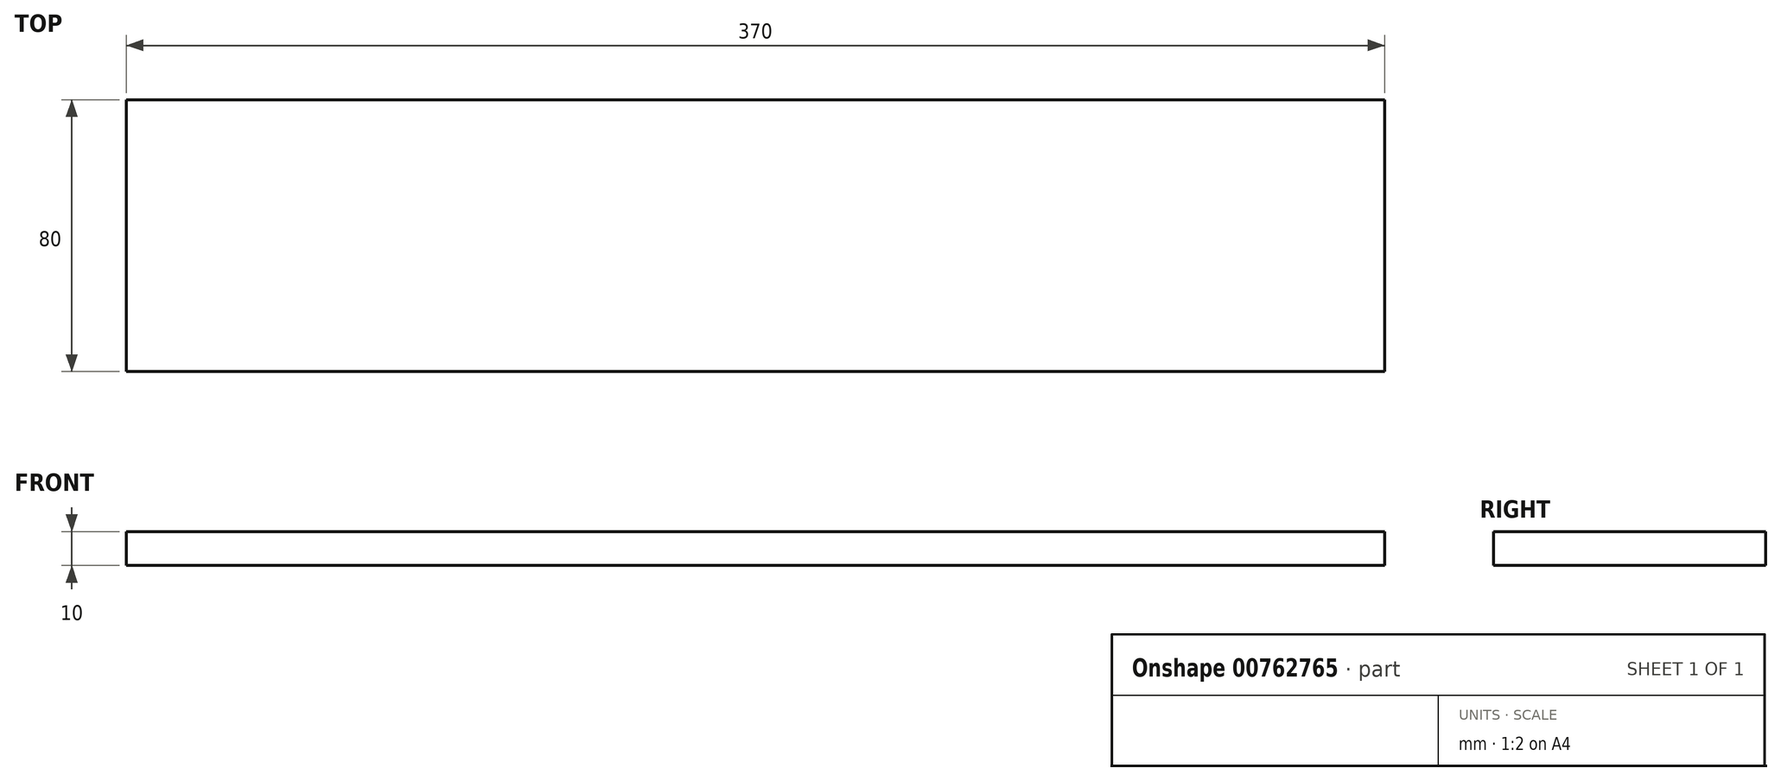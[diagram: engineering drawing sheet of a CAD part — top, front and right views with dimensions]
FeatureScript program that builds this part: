
annotation { "Feature Type Name" : "Feature", "Feature Type Description" : "" }
export const myFeature = defineFeature(function(context is Context, id is Id, definition is map)
    precondition{}
    {
        {
            var Q0;
            Q0=qCreatedBy(makeId("Top.planeOp"),FACE);
            var sketch = newSketch(context, id + "F0", { "sketchPlane" : qUnion([Q0])});
            skLineSegment(sketch, "E0.bottom", {"start": v(185, 40) * mm, "end": v(-185, 40) * mm});
            skLineSegment(sketch, "E0.top", {"start": v(185, -40) * mm, "end": v(-185, -40) * mm});
            skLineSegment(sketch, "E0.left", {"start": v(185, 40) * mm, "end": v(185, -40) * mm});
            skLineSegment(sketch, "E0.right", {"start": v(-185, 40) * mm, "end": v(-185, -40) * mm});
            skPoint(sketch, "E0.middle", {"position": v(0, 0) * mm});
            skSolve(sketch);
        }
        {
            var Q0;
            Q0 = qSketchRegion(id + "F0", true);
            extrude(context, id + "F1", {"entities" : qUnion([Q0]), "depth" : 10 * mm, "offsetDistance" : 25 * mm});
        }
    });
